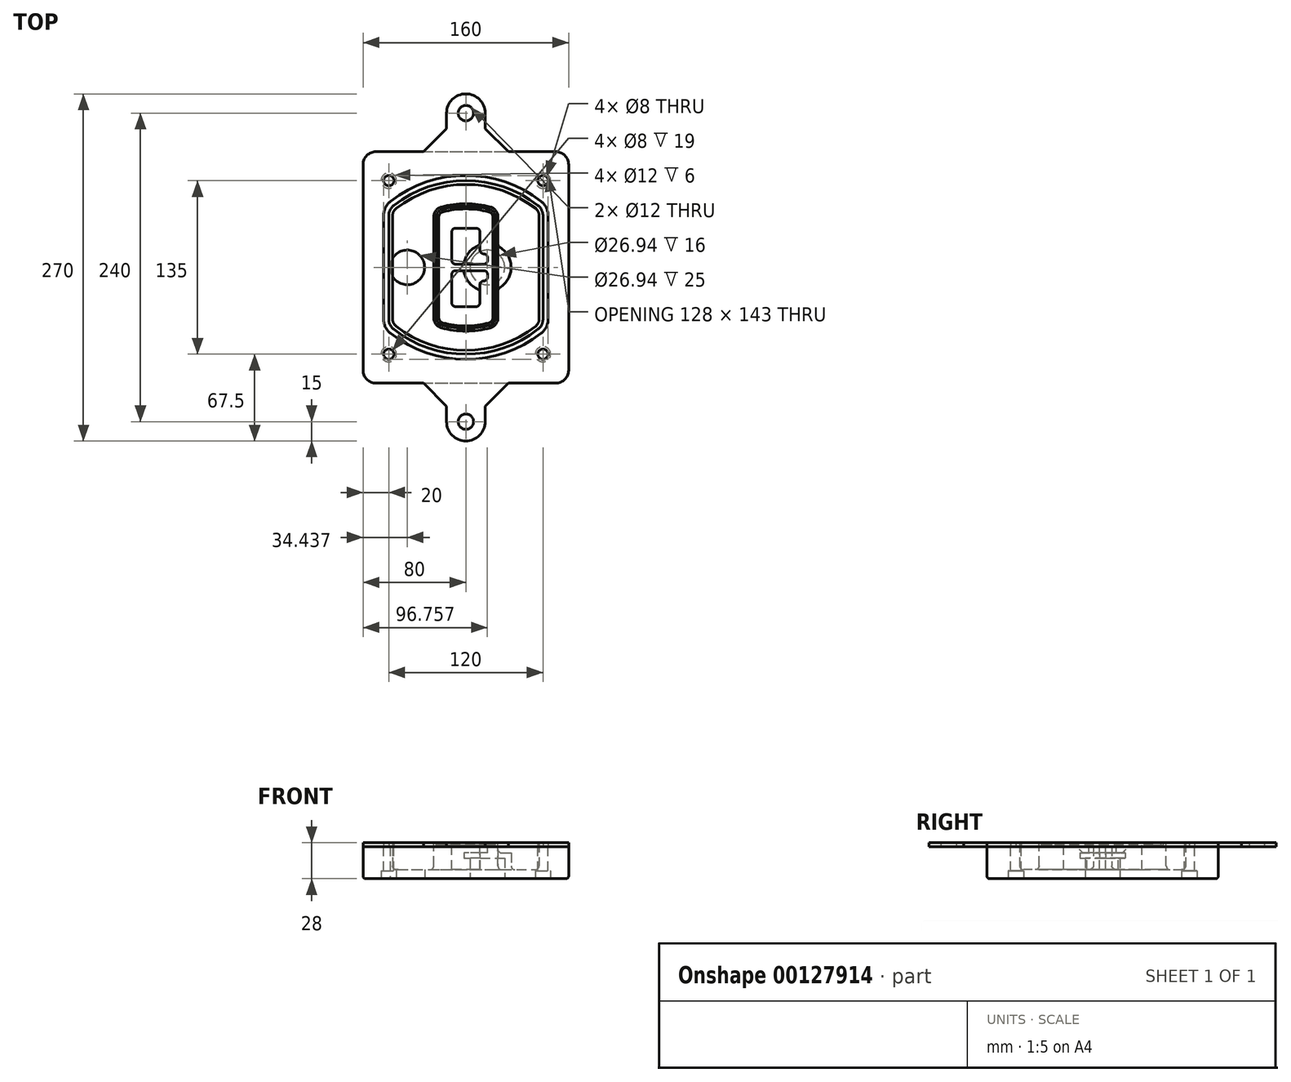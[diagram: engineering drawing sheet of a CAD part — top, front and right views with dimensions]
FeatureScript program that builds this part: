
annotation { "Feature Type Name" : "Feature", "Feature Type Description" : "" }
export const myFeature = defineFeature(function(context is Context, id is Id, definition is map)
    precondition{}
    {
        {
            var Q0;
            Q0=qCreatedBy(makeId("Top.planeOp"),FACE);
            var sketch = newSketch(context, id + "F0", { "sketchPlane" : qUnion([Q0])});
            skPoint(sketch, "E0.rect.middle", {"position": v(0, 0) * mm});
            skLineSegment(sketch, "E1.bottom", {"start": v(-70, -90) * mm, "end": v(70, -90) * mm});
            skLineSegment(sketch, "E1.top", {"start": v(-70, 90) * mm, "end": v(70, 90) * mm});
            skLineSegment(sketch, "E1.left", {"start": v(-80, -80) * mm, "end": v(-80, 80) * mm});
            skLineSegment(sketch, "E1.right", {"start": v(80, -80) * mm, "end": v(80, 80) * mm});
            skLineSegment(sketch, "E2", {"start": v(-80, 90) * mm, "end": v(80, -90) * mm, "construction": true});
            skLineSegment(sketch, "E3", {"start": v(80, 90) * mm, "end": v(-80, -90) * mm, "construction": true});
            skCircle(sketch, "E4", {"center": v(-60, 67.5) * mm, "radius": 4 * mm});
            skCircle(sketch, "E5", {"center": v(60, 67.5) * mm, "radius": 4 * mm});
            skCircle(sketch, "E6", {"center": v(60, -67.5) * mm, "radius": 4 * mm});
            skCircle(sketch, "E7", {"center": v(-60, -67.5) * mm, "radius": 4 * mm});
            skLineSegment(sketch, "E8", {"start": v(-60, 67.5) * mm, "end": v(60, 67.5) * mm, "construction": true});
            skLineSegment(sketch, "E9", {"start": v(60, 67.5) * mm, "end": v(60, -67.5) * mm, "construction": true});
            skLineSegment(sketch, "E10", {"start": v(60, -67.5) * mm, "end": v(-60, -67.5) * mm, "construction": true});
            skLineSegment(sketch, "E11", {"start": v(-60, -67.5) * mm, "end": v(-60, 67.5) * mm, "construction": true});
            skLineSegment(sketch, "E12", {"start": v(-60, 40.3) * mm, "end": v(-60, -40.3) * mm});
            skLineSegment(sketch, "E13", {"start": v(60, 40.3) * mm, "end": v(60, -40.3) * mm});
            skArc(sketch, "E14", {"start": v(56.15, 48.18) * mm, "mid": v(0, 67.5) * mm, "end": v(-56.15, 48.18) * mm});
            skArc(sketch, "E15", {"start": v(-56.15, -48.18) * mm, "mid": v(0, -67.5) * mm, "end": v(56.15, -48.18) * mm});
            skLineSegment(sketch, "E16", {"start": v(-60, 0) * mm, "end": v(60, 0) * mm, "construction": true});
            skPoint(sketch, "E17.visualSharp", {"position": v(-60, -45) * mm});
            skArc(sketch, "E17.filletArc", {"start": v(-60, -40.3) * mm, "mid": v(-58.99, -44.68) * mm, "end": v(-56.15, -48.18) * mm});
            skPoint(sketch, "E18.visualSharp", {"position": v(-60, 45) * mm});
            skArc(sketch, "E18.filletArc", {"start": v(-56.15, 48.18) * mm, "mid": v(-58.99, 44.68) * mm, "end": v(-60, 40.3) * mm});
            skPoint(sketch, "E19.visualSharp", {"position": v(60, 45) * mm});
            skArc(sketch, "E19.filletArc", {"start": v(60, 40.3) * mm, "mid": v(58.99, 44.68) * mm, "end": v(56.15, 48.18) * mm});
            skPoint(sketch, "E20.visualSharp", {"position": v(60, -45) * mm});
            skArc(sketch, "E20.filletArc", {"start": v(56.15, -48.18) * mm, "mid": v(58.99, -44.68) * mm, "end": v(60, -40.3) * mm});
            skPoint(sketch, "E21.visualSharp", {"position": v(-80, 90) * mm});
            skArc(sketch, "E21.filletArc", {"start": v(-70, 90) * mm, "mid": v(-77.07, 87.07) * mm, "end": v(-80, 80) * mm});
            skPoint(sketch, "E22.visualSharp", {"position": v(80, 90) * mm});
            skArc(sketch, "E22.filletArc", {"start": v(80, 80) * mm, "mid": v(77.07, 87.07) * mm, "end": v(70, 90) * mm});
            skPoint(sketch, "E23.visualSharp", {"position": v(80, -90) * mm});
            skArc(sketch, "E23.filletArc", {"start": v(70, -90) * mm, "mid": v(77.07, -87.07) * mm, "end": v(80, -80) * mm});
            skPoint(sketch, "E24.visualSharp", {"position": v(-80, -90) * mm});
            skArc(sketch, "E24.filletArc", {"start": v(-80, -80) * mm, "mid": v(-77.07, -87.07) * mm, "end": v(-70, -90) * mm});
            skArc(sketch, "E25.0", {"start": v(57, 40.3) * mm, "mid": v(56.3, 43.36) * mm, "end": v(54.3, 45.81) * mm});
            skLineSegment(sketch, "E25.1", {"start": v(57, 40.3) * mm, "end": v(57, -40.3) * mm});
            skArc(sketch, "E25.2", {"start": v(54.3, -45.81) * mm, "mid": v(56.3, -43.36) * mm, "end": v(57, -40.3) * mm});
            skArc(sketch, "E25.3", {"start": v(-54.3, -45.81) * mm, "mid": v(0, -64.5) * mm, "end": v(54.3, -45.81) * mm});
            skArc(sketch, "E25.4", {"start": v(-57, -40.3) * mm, "mid": v(-56.3, -43.36) * mm, "end": v(-54.3, -45.81) * mm});
            skArc(sketch, "E25.5", {"start": v(54.3, 45.81) * mm, "mid": v(0, 64.5) * mm, "end": v(-54.3, 45.81) * mm});
            skLineSegment(sketch, "E25.6", {"start": v(-57, 40.3) * mm, "end": v(-57, -40.3) * mm});
            skArc(sketch, "E25.7", {"start": v(-54.3, 45.81) * mm, "mid": v(-56.3, 43.36) * mm, "end": v(-57, 40.3) * mm});
            skArc(sketch, "E26.0", {"start": v(-58.62, 51.33) * mm, "mid": v(-62.58, 46.43) * mm, "end": v(-64, 40.3) * mm});
            skArc(sketch, "E26.1", {"start": v(58.62, 51.33) * mm, "mid": v(0, 71.5) * mm, "end": v(-58.62, 51.33) * mm});
            skArc(sketch, "E26.2", {"start": v(64, 40.3) * mm, "mid": v(62.58, 46.43) * mm, "end": v(58.62, 51.33) * mm});
            skLineSegment(sketch, "E26.3", {"start": v(64, 40.3) * mm, "end": v(64, -40.3) * mm});
            skArc(sketch, "E26.4", {"start": v(58.62, -51.33) * mm, "mid": v(62.58, -46.43) * mm, "end": v(64, -40.3) * mm});
            skLineSegment(sketch, "E26.5", {"start": v(-64, 40.3) * mm, "end": v(-64, -40.3) * mm});
            skArc(sketch, "E26.6", {"start": v(-58.62, -51.33) * mm, "mid": v(0, -71.5) * mm, "end": v(58.62, -51.33) * mm});
            skArc(sketch, "E26.7", {"start": v(-64, -40.3) * mm, "mid": v(-62.58, -46.43) * mm, "end": v(-58.62, -51.33) * mm});
            skSolve(sketch);
        }
        {
            var Q0;
            Q0=makeQuery(id+"F0.imprint","IMPRINT",FACE,{"disambiguationData":[TD([[makeQuery(id+"F0.imprint","IMPRINT",EDGE,{"derivedFrom":sQuery(id+"F0.wireOp",EDGE,"E1.bottom")}),1.0]])]});
            var Q1;
            Q1=makeQuery(id+"F0.imprint","IMPRINT",FACE,{"disambiguationData":[TD([[makeQuery(id+"F0.imprint","IMPRINT",EDGE,{"derivedFrom":sQuery(id+"F0.wireOp",EDGE,"E12")}),1.0]])]});
            var Q2;
            Q2=makeQuery(id+"F0.imprint","IMPRINT",FACE,{"disambiguationData":[TD([[makeQuery(id+"F0.imprint","IMPRINT",EDGE,{"derivedFrom":sQuery(id+"F0.wireOp",EDGE,"E25.0")}),1.0]])]});
            var Q3;
            Q3=makeQuery(id+"F0.imprint","IMPRINT",FACE,{"disambiguationData":[TD([[makeQuery(id+"F0.imprint","IMPRINT",EDGE,{"derivedFrom":sQuery(id+"F0.wireOp",EDGE,"E12")}),-1.0]])]});
            extrude(context, id + "F1", {"entities" : qUnion([Q0, Q1, Q2, Q3]), "oppositeDirection" : true, "depth" : 25 * mm});
        }
        {
            var Q0;
            Q0=makeQuery(id+"F0.imprint","IMPRINT",FACE,{"disambiguationData":[TD([[makeQuery(id+"F0.imprint","IMPRINT",EDGE,{"derivedFrom":sQuery(id+"F0.wireOp",EDGE,"E12")}),1.0]])]});
            extrude(context, id + "F2", {"entities" : qUnion([Q0]), "operationType" : NewBodyOperationType.ADD, "depth" : 3 * mm});
        }
        {
            var Q0;
            Q0=makeQuery(id+"F0.imprint","IMPRINT",FACE,{"disambiguationData":[TD([[makeQuery(id+"F0.imprint","IMPRINT",EDGE,{"derivedFrom":sQuery(id+"F0.wireOp",EDGE,"E25.0")}),1.0]])]});
            extrude(context, id + "F3", {"entities" : qUnion([Q0]), "operationType" : NewBodyOperationType.REMOVE, "oppositeDirection" : true, "depth" : 18 * mm});
        }
        {
            var Q0;
            Q0=makeQuery(id+"F2.opExtrude","CAP_FACE",FACE,{"disambiguationData":[OSD([sQuery(id+"F0.wireOp",EDGE,"E12"),sQuery(id+"F0.wireOp",EDGE,"E13"),sQuery(id+"F0.wireOp",EDGE,"E14"),sQuery(id+"F0.wireOp",EDGE,"E15"),sQuery(id+"F0.wireOp",EDGE,"E17.filletArc"),sQuery(id+"F0.wireOp",EDGE,"E18.filletArc"),sQuery(id+"F0.wireOp",EDGE,"E19.filletArc"),sQuery(id+"F0.wireOp",EDGE,"E20.filletArc"),sQuery(id+"F0.wireOp",EDGE,"E25.0"),sQuery(id+"F0.wireOp",EDGE,"E25.1"),sQuery(id+"F0.wireOp",EDGE,"E25.2"),sQuery(id+"F0.wireOp",EDGE,"E25.3"),sQuery(id+"F0.wireOp",EDGE,"E25.4"),sQuery(id+"F0.wireOp",EDGE,"E25.5"),sQuery(id+"F0.wireOp",EDGE,"E25.6"),sQuery(id+"F0.wireOp",EDGE,"E25.7")])],"isStart":false});
            var sketch = newSketch(context, id + "F4", { "sketchPlane" : qUnion([Q0])});
            skArc(sketch, "E27.0", {"start": v(-19.08, -46.97) * mm, "mid": v(0, -49.5) * mm, "end": v(19.08, -46.97) * mm});
            skArc(sketch, "E28.0", {"start": v(19.08, 46.97) * mm, "mid": v(0, 49.5) * mm, "end": v(-19.08, 46.97) * mm});
            skLineSegment(sketch, "E29", {"start": v(-25, 39.25) * mm, "end": v(-25, -39.25) * mm});
            skLineSegment(sketch, "E30", {"start": v(25, 39.25) * mm, "end": v(25, -39.25) * mm});
            skLineSegment(sketch, "E31", {"start": v(-25, 45.1) * mm, "end": v(25, 45.1) * mm, "construction": true});
            skLineSegment(sketch, "E32", {"start": v(-25, -45.1) * mm, "end": v(25, -45.1) * mm, "construction": true});
            skPoint(sketch, "E33.visualSharp", {"position": v(-25, 45.1) * mm});
            skArc(sketch, "E33.filletArc", {"start": v(-19.08, 46.97) * mm, "mid": v(-23.35, 44.11) * mm, "end": v(-25, 39.25) * mm});
            skPoint(sketch, "E34.visualSharp", {"position": v(25, 45.1) * mm});
            skArc(sketch, "E34.filletArc", {"start": v(25, 39.25) * mm, "mid": v(23.35, 44.11) * mm, "end": v(19.08, 46.97) * mm});
            skPoint(sketch, "E35.visualSharp", {"position": v(25, -45.1) * mm});
            skArc(sketch, "E35.filletArc", {"start": v(19.08, -46.97) * mm, "mid": v(23.35, -44.11) * mm, "end": v(25, -39.25) * mm});
            skPoint(sketch, "E36.visualSharp", {"position": v(-25, -45.1) * mm});
            skArc(sketch, "E36.filletArc", {"start": v(-25, -39.25) * mm, "mid": v(-23.35, -44.11) * mm, "end": v(-19.08, -46.97) * mm});
            skArc(sketch, "E37.0", {"start": v(54.3, 45.81) * mm, "mid": v(0, 64.5) * mm, "end": v(-54.3, 45.81) * mm});
            skArc(sketch, "E37.1", {"start": v(-54.3, 45.81) * mm, "mid": v(-56.3, 43.36) * mm, "end": v(-57, 40.3) * mm});
            skLineSegment(sketch, "E37.2", {"start": v(-57, 40.3) * mm, "end": v(-57, -40.3) * mm});
            skArc(sketch, "E37.3", {"start": v(-57, -40.3) * mm, "mid": v(-56.3, -43.36) * mm, "end": v(-54.3, -45.81) * mm});
            skArc(sketch, "E37.4", {"start": v(-54.3, -45.81) * mm, "mid": v(0, -64.5) * mm, "end": v(54.3, -45.81) * mm});
            skArc(sketch, "E37.5", {"start": v(54.3, -45.81) * mm, "mid": v(56.3, -43.36) * mm, "end": v(57, -40.3) * mm});
            skLineSegment(sketch, "E37.6", {"start": v(57, 40.3) * mm, "end": v(57, -40.3) * mm});
            skArc(sketch, "E37.7", {"start": v(57, 40.3) * mm, "mid": v(56.3, 43.36) * mm, "end": v(54.3, 45.81) * mm});
            skLineSegment(sketch, "E38.0", {"start": v(23, 39.25) * mm, "end": v(23, -39.25) * mm});
            skArc(sketch, "E38.1", {"start": v(18.56, -45.04) * mm, "mid": v(21.76, -42.9) * mm, "end": v(23, -39.25) * mm});
            skArc(sketch, "E38.2", {"start": v(-18.56, -45.04) * mm, "mid": v(0, -47.5) * mm, "end": v(18.56, -45.04) * mm});
            skArc(sketch, "E38.3", {"start": v(-23, -39.25) * mm, "mid": v(-21.76, -42.9) * mm, "end": v(-18.56, -45.04) * mm});
            skLineSegment(sketch, "E38.4", {"start": v(-23, 39.25) * mm, "end": v(-23, -39.25) * mm});
            skArc(sketch, "E38.5", {"start": v(23, 39.25) * mm, "mid": v(21.76, 42.9) * mm, "end": v(18.56, 45.04) * mm});
            skArc(sketch, "E38.6", {"start": v(-18.56, 45.04) * mm, "mid": v(-21.76, 42.9) * mm, "end": v(-23, 39.25) * mm});
            skArc(sketch, "E38.7", {"start": v(18.56, 45.04) * mm, "mid": v(0, 47.5) * mm, "end": v(-18.56, 45.04) * mm});
            skArc(sketch, "E39.0", {"start": v(21, 39.25) * mm, "mid": v(20.18, 41.68) * mm, "end": v(18.04, 43.1) * mm});
            skLineSegment(sketch, "E39.1", {"start": v(21, 39.25) * mm, "end": v(21, -39.25) * mm});
            skArc(sketch, "E39.2", {"start": v(18.04, -43.1) * mm, "mid": v(20.18, -41.68) * mm, "end": v(21, -39.25) * mm});
            skArc(sketch, "E39.3", {"start": v(-18.04, -43.1) * mm, "mid": v(0, -45.5) * mm, "end": v(18.04, -43.1) * mm});
            skArc(sketch, "E39.4", {"start": v(-21, -39.25) * mm, "mid": v(-20.18, -41.68) * mm, "end": v(-18.04, -43.1) * mm});
            skArc(sketch, "E39.5", {"start": v(18.04, 43.1) * mm, "mid": v(0, 45.5) * mm, "end": v(-18.04, 43.1) * mm});
            skLineSegment(sketch, "E39.6", {"start": v(-21, 39.25) * mm, "end": v(-21, -39.25) * mm});
            skArc(sketch, "E39.7", {"start": v(-18.04, 43.1) * mm, "mid": v(-20.18, 41.68) * mm, "end": v(-21, 39.25) * mm});
            skLineSegment(sketch, "E40", {"start": v(-25, 0) * mm, "end": v(25, 0) * mm, "construction": true});
            skLineSegment(sketch, "E41", {"start": v(-11, 5.5) * mm, "end": v(-11, 27.5) * mm});
            skLineSegment(sketch, "E42", {"start": v(-8, 30.5) * mm, "end": v(8, 30.5) * mm});
            skLineSegment(sketch, "E43", {"start": v(11, 27.5) * mm, "end": v(11, 13.5) * mm});
            skLineSegment(sketch, "E44", {"start": v(14, 10.5) * mm, "end": v(14, 10.5) * mm});
            skLineSegment(sketch, "E45", {"start": v(17, 7.5) * mm, "end": v(17, 5.5) * mm});
            skLineSegment(sketch, "E46", {"start": v(14, 2.5) * mm, "end": v(-8, 2.5) * mm});
            skPoint(sketch, "E47.visualSharp", {"position": v(-11, 30.5) * mm});
            skArc(sketch, "E47.filletArc", {"start": v(-8, 30.5) * mm, "mid": v(-10.12, 29.62) * mm, "end": v(-11, 27.5) * mm});
            skPoint(sketch, "E48.visualSharp", {"position": v(11, 30.5) * mm});
            skArc(sketch, "E48.filletArc", {"start": v(11, 27.5) * mm, "mid": v(10.12, 29.62) * mm, "end": v(8, 30.5) * mm});
            skPoint(sketch, "E49.visualSharp", {"position": v(11, 10.5) * mm});
            skArc(sketch, "E49.filletArc", {"start": v(11, 13.5) * mm, "mid": v(11.88, 11.38) * mm, "end": v(14, 10.5) * mm});
            skPoint(sketch, "E50.visualSharp", {"position": v(17, 10.5) * mm});
            skArc(sketch, "E50.filletArc", {"start": v(17, 7.5) * mm, "mid": v(16.12, 9.62) * mm, "end": v(14, 10.5) * mm});
            skPoint(sketch, "E51.visualSharp", {"position": v(17, 2.5) * mm});
            skArc(sketch, "E51.filletArc", {"start": v(14, 2.5) * mm, "mid": v(16.12, 3.38) * mm, "end": v(17, 5.5) * mm});
            skPoint(sketch, "E52.visualSharp", {"position": v(-11, 2.5) * mm});
            skArc(sketch, "E52.filletArc", {"start": v(-11, 5.5) * mm, "mid": v(-10.12, 3.38) * mm, "end": v(-8, 2.5) * mm});
            skLineSegment(sketch, "E53.0.MirrorCS", {"start": v(14, -2.5) * mm, "end": v(-8, -2.5) * mm});
            skArc(sketch, "E54.0.MirrorCS", {"start": v(-11, -5.5) * mm, "mid": v(-10.12, -3.38) * mm, "end": v(-8, -2.5) * mm});
            skLineSegment(sketch, "E55.0.MirrorCS", {"start": v(-11, -5.5) * mm, "end": v(-11, -27.5) * mm});
            skArc(sketch, "E56.0.MirrorCS", {"start": v(-8, -30.5) * mm, "mid": v(-10.12, -29.62) * mm, "end": v(-11, -27.5) * mm});
            skLineSegment(sketch, "E57.0.MirrorCS", {"start": v(-8, -30.5) * mm, "end": v(8, -30.5) * mm});
            skArc(sketch, "E58.0.MirrorCS", {"start": v(11, -27.5) * mm, "mid": v(10.12, -29.62) * mm, "end": v(8, -30.5) * mm});
            skLineSegment(sketch, "E59.0.MirrorCS", {"start": v(11, -27.5) * mm, "end": v(11, -13.5) * mm});
            skArc(sketch, "E60.0.MirrorCS", {"start": v(11, -13.5) * mm, "mid": v(11.88, -11.38) * mm, "end": v(14, -10.5) * mm});
            skArc(sketch, "E61.0.MirrorCS", {"start": v(17, -7.5) * mm, "mid": v(16.12, -9.62) * mm, "end": v(14, -10.5) * mm});
            skLineSegment(sketch, "E62.0.MirrorCS", {"start": v(17, -7.5) * mm, "end": v(17, -5.5) * mm});
            skArc(sketch, "E63.0.MirrorCS", {"start": v(14, -2.5) * mm, "mid": v(16.12, -3.38) * mm, "end": v(17, -5.5) * mm});
            skSolve(sketch);
        }
        {
            var Q0;
            Q0=makeQuery(id+"F4.imprint","IMPRINT",FACE,{"disambiguationData":[TD([[makeQuery(id+"F4.imprint","IMPRINT",EDGE,{"derivedFrom":sQuery(id+"F4.wireOp",EDGE,"E27.0")}),1.0]])]});
            var Q1;
            Q1=makeQuery(id+"F4.imprint","IMPRINT",FACE,{"disambiguationData":[TD([[makeQuery(id+"F4.imprint","IMPRINT",EDGE,{"derivedFrom":sQuery(id+"F4.wireOp",EDGE,"E38.0")}),-1.0]])]});
            var Q2;
            Q2=makeQuery(id+"F4.imprint","IMPRINT",FACE,{"disambiguationData":[TD([[makeQuery(id+"F4.imprint","IMPRINT",EDGE,{"derivedFrom":sQuery(id+"F4.wireOp",EDGE,"E39.0")}),1.0]])]});
            extrude(context, id + "F5", {"entities" : qUnion([Q0, Q1, Q2]), "operationType" : NewBodyOperationType.ADD, "endBound" : BoundingType.UP_TO_NEXT, "oppositeDirection" : true, "depth" : 25 * mm});
        }
        {
            var Q0;
            Q0=makeQuery(id+"F4.imprint","IMPRINT",FACE,{"disambiguationData":[TD([[makeQuery(id+"F4.imprint","IMPRINT",EDGE,{"derivedFrom":sQuery(id+"F4.wireOp",EDGE,"E38.0")}),-1.0]])]});
            extrude(context, id + "F6", {"entities" : qUnion([Q0]), "operationType" : NewBodyOperationType.REMOVE, "oppositeDirection" : true, "depth" : 2 * mm});
        }
        {
            var Q0;
            Q0=makeQuery(id+"F1.opExtrude","CAP_FACE",FACE,{"disambiguationData":[OSD([sQuery(id+"F0.wireOp",EDGE,"E1.bottom"),sQuery(id+"F0.wireOp",EDGE,"E1.top"),sQuery(id+"F0.wireOp",EDGE,"E1.left"),sQuery(id+"F0.wireOp",EDGE,"E1.right"),sQuery(id+"F0.wireOp",EDGE,"E4"),sQuery(id+"F0.wireOp",EDGE,"E5"),sQuery(id+"F0.wireOp",EDGE,"E6"),sQuery(id+"F0.wireOp",EDGE,"E7"),sQuery(id+"F0.wireOp",EDGE,"E21.filletArc"),sQuery(id+"F0.wireOp",EDGE,"E22.filletArc"),sQuery(id+"F0.wireOp",EDGE,"E23.filletArc"),sQuery(id+"F0.wireOp",EDGE,"E24.filletArc")])],"isStart":false});
            var sketch = newSketch(context, id + "F7", { "sketchPlane" : qUnion([Q0])});
            skCircle(sketch, "E64", {"center": v(16.76, 0) * mm, "radius": 13.47 * mm});
            skCircle(sketch, "E65", {"center": v(-45.56, 0) * mm, "radius": 13.47 * mm});
            skLineSegment(sketch, "E66", {"start": v(80, 0) * mm, "end": v(-80, 0) * mm});
            skCircle(sketch, "E67", {"center": v(16.76, 0) * mm, "radius": 18.47 * mm});
            skCircle(sketch, "E68", {"center": v(60, -67.5) * mm, "radius": 6 * mm});
            skCircle(sketch, "E69", {"center": v(-60, -67.5) * mm, "radius": 6 * mm});
            skCircle(sketch, "E70", {"center": v(-60, 67.5) * mm, "radius": 6 * mm});
            skCircle(sketch, "E71", {"center": v(60, 67.5) * mm, "radius": 6 * mm});
            skSolve(sketch);
        }
        {
            var Q0;
            {var subQ1=sQuery(id+"F7.wireOp",EDGE,"E66");var subQ4=sQuery(id+"F7.wireOp",EDGE,"E64");var subQ6=makeQuery(id+"F7.imprint","INTERSECT",VERTEX,{"disambiguationData":[OD(0.0)],"derivedFrom":[subQ4,subQ1]});Q0=makeQuery(id+"F7.imprint","IMPRINT",FACE,{"disambiguationData":[TD([[makeQuery(id+"F7.imprint","IMPRINT",EDGE,{"disambiguationData":[TD([[subQ6,-1.0]])],"derivedFrom":subQ4}),-1.0]])]});}
            var Q1;
            {var subQ0=sQuery(id+"F7.wireOp",EDGE,"E66");var subQ1=sQuery(id+"F7.wireOp",EDGE,"E64");var subQ3=makeQuery(id+"F7.imprint","INTERSECT",VERTEX,{"disambiguationData":[OD(0.0)],"derivedFrom":[subQ1,subQ0]});Q1=makeQuery(id+"F7.imprint","IMPRINT",FACE,{"disambiguationData":[TD([[makeQuery(id+"F7.imprint","IMPRINT",EDGE,{"disambiguationData":[TD([[subQ3,-1.0]])],"derivedFrom":subQ1}),1.0]])]});}
            var Q2;
            {var subQ0=sQuery(id+"F7.wireOp",EDGE,"E66");var subQ1=sQuery(id+"F7.wireOp",EDGE,"E64");var subQ3=makeQuery(id+"F7.imprint","INTERSECT",VERTEX,{"disambiguationData":[OD(0.0)],"derivedFrom":[subQ1,subQ0]});Q2=makeQuery(id+"F7.imprint","IMPRINT",FACE,{"disambiguationData":[TD([[makeQuery(id+"F7.imprint","IMPRINT",EDGE,{"disambiguationData":[TD([[subQ3,1.0]])],"derivedFrom":subQ1}),1.0]])]});}
            var Q3;
            {var subQ1=sQuery(id+"F7.wireOp",EDGE,"E66");var subQ4=sQuery(id+"F7.wireOp",EDGE,"E64");var subQ6=makeQuery(id+"F7.imprint","INTERSECT",VERTEX,{"disambiguationData":[OD(0.0)],"derivedFrom":[subQ4,subQ1]});Q3=makeQuery(id+"F7.imprint","IMPRINT",FACE,{"disambiguationData":[TD([[makeQuery(id+"F7.imprint","IMPRINT",EDGE,{"disambiguationData":[TD([[subQ6,1.0]])],"derivedFrom":subQ4}),-1.0]])]});}
            extrude(context, id + "F8", {"entities" : qUnion([Q0, Q1, Q2, Q3]), "operationType" : NewBodyOperationType.ADD, "oppositeDirection" : true, "depth" : 20 * mm});
        }
        {
            var Q0;
            {var subQ0=sQuery(id+"F7.wireOp",EDGE,"E66");var subQ1=sQuery(id+"F7.wireOp",EDGE,"E64");var subQ3=makeQuery(id+"F7.imprint","INTERSECT",VERTEX,{"disambiguationData":[OD(0.0)],"derivedFrom":[subQ1,subQ0]});Q0=makeQuery(id+"F7.imprint","IMPRINT",FACE,{"disambiguationData":[TD([[makeQuery(id+"F7.imprint","IMPRINT",EDGE,{"disambiguationData":[TD([[subQ3,-1.0]])],"derivedFrom":subQ1}),1.0]])]});}
            var Q1;
            {var subQ0=sQuery(id+"F7.wireOp",EDGE,"E66");var subQ1=sQuery(id+"F7.wireOp",EDGE,"E64");var subQ3=makeQuery(id+"F7.imprint","INTERSECT",VERTEX,{"disambiguationData":[OD(0.0)],"derivedFrom":[subQ1,subQ0]});Q1=makeQuery(id+"F7.imprint","IMPRINT",FACE,{"disambiguationData":[TD([[makeQuery(id+"F7.imprint","IMPRINT",EDGE,{"disambiguationData":[TD([[subQ3,1.0]])],"derivedFrom":subQ1}),1.0]])]});}
            extrude(context, id + "F9", {"entities" : qUnion([Q0, Q1]), "operationType" : NewBodyOperationType.REMOVE, "oppositeDirection" : true, "depth" : 16 * mm});
        }
        {
            var Q0;
            {var subQ0=sQuery(id+"F7.wireOp",EDGE,"E66");var subQ1=sQuery(id+"F7.wireOp",EDGE,"E65");var subQ3=makeQuery(id+"F7.imprint","INTERSECT",VERTEX,{"disambiguationData":[OD(0.0)],"derivedFrom":[subQ1,subQ0]});Q0=makeQuery(id+"F7.imprint","IMPRINT",FACE,{"disambiguationData":[TD([[makeQuery(id+"F7.imprint","IMPRINT",EDGE,{"disambiguationData":[TD([[subQ3,-1.0]])],"derivedFrom":subQ1}),1.0]])]});}
            var Q1;
            {var subQ0=sQuery(id+"F7.wireOp",EDGE,"E66");var subQ1=sQuery(id+"F7.wireOp",EDGE,"E65");var subQ3=makeQuery(id+"F7.imprint","INTERSECT",VERTEX,{"disambiguationData":[OD(0.0)],"derivedFrom":[subQ1,subQ0]});Q1=makeQuery(id+"F7.imprint","IMPRINT",FACE,{"disambiguationData":[TD([[makeQuery(id+"F7.imprint","IMPRINT",EDGE,{"disambiguationData":[TD([[subQ3,1.0]])],"derivedFrom":subQ1}),1.0]])]});}
            extrude(context, id + "F10", {"entities" : qUnion([Q0, Q1]), "operationType" : NewBodyOperationType.REMOVE, "oppositeDirection" : true, "depth" : 25 * mm});
        }
        {
            var Q0;
            Q0=makeQuery(id+"F7.imprint","IMPRINT",FACE,{"disambiguationData":[TD([[makeQuery(id+"F7.imprint","IMPRINT",EDGE,{"derivedFrom":sQuery(id+"F7.wireOp",EDGE,"E68")}),1.0]])]});
            var Q1;
            Q1=makeQuery(id+"F7.imprint","IMPRINT",FACE,{"disambiguationData":[TD([[makeQuery(id+"F7.imprint","IMPRINT",EDGE,{"derivedFrom":makeQuery(id+"F1.opExtrude","CAP_EDGE",EDGE,{"disambiguationData":[OSD([sQuery(id+"F0.wireOp",EDGE,"E5")])],"isStart":false})}),-1.0]])]});
            var Q2;
            Q2=makeQuery(id+"F7.imprint","IMPRINT",FACE,{"disambiguationData":[TD([[makeQuery(id+"F7.imprint","IMPRINT",EDGE,{"derivedFrom":sQuery(id+"F7.wireOp",EDGE,"E69")}),1.0]])]});
            var Q3;
            Q3=makeQuery(id+"F7.imprint","IMPRINT",FACE,{"disambiguationData":[TD([[makeQuery(id+"F7.imprint","IMPRINT",EDGE,{"derivedFrom":makeQuery(id+"F1.opExtrude","CAP_EDGE",EDGE,{"disambiguationData":[OSD([sQuery(id+"F0.wireOp",EDGE,"E4")])],"isStart":false})}),-1.0]])]});
            var Q4;
            Q4=makeQuery(id+"F7.imprint","IMPRINT",FACE,{"disambiguationData":[TD([[makeQuery(id+"F7.imprint","IMPRINT",EDGE,{"derivedFrom":sQuery(id+"F7.wireOp",EDGE,"E70")}),1.0]])]});
            var Q5;
            Q5=makeQuery(id+"F7.imprint","IMPRINT",FACE,{"disambiguationData":[TD([[makeQuery(id+"F7.imprint","IMPRINT",EDGE,{"derivedFrom":makeQuery(id+"F1.opExtrude","CAP_EDGE",EDGE,{"disambiguationData":[OSD([sQuery(id+"F0.wireOp",EDGE,"E7")])],"isStart":false})}),-1.0]])]});
            var Q6;
            Q6=makeQuery(id+"F7.imprint","IMPRINT",FACE,{"disambiguationData":[TD([[makeQuery(id+"F7.imprint","IMPRINT",EDGE,{"derivedFrom":sQuery(id+"F7.wireOp",EDGE,"E71")}),1.0]])]});
            var Q7;
            Q7=makeQuery(id+"F7.imprint","IMPRINT",FACE,{"disambiguationData":[TD([[makeQuery(id+"F7.imprint","IMPRINT",EDGE,{"derivedFrom":makeQuery(id+"F1.opExtrude","CAP_EDGE",EDGE,{"disambiguationData":[OSD([sQuery(id+"F0.wireOp",EDGE,"E6")])],"isStart":false})}),-1.0]])]});
            extrude(context, id + "F11", {"entities" : qUnion([Q0, Q1, Q2, Q3, Q4, Q5, Q6, Q7]), "operationType" : NewBodyOperationType.REMOVE, "oppositeDirection" : true, "depth" : 6 * mm});
        }
        {
            var Q0;
            Q0=makeQuery(id+"F9.boolean.opBoolean","COPY",FACE,{"derivedFrom":makeQuery(id+"F9.opExtrude","CAP_FACE",FACE,{"disambiguationData":[OSD([sQuery(id+"F7.wireOp",EDGE,"E64")])],"isStart":false})});
            var sketch = newSketch(context, id + "F12", { "sketchPlane" : qUnion([Q0])});
            skArc(sketch, "E72.0", {"start": v(11, 17.55) * mm, "mid": v(2.57, 11.82) * mm, "end": v(-1.54, 2.5) * mm});
            skArc(sketch, "E72.1", {"start": v(-1.54, -2.5) * mm, "mid": v(2.57, -11.82) * mm, "end": v(11, -17.55) * mm});
            skLineSegment(sketch, "E73", {"start": v(-1.54, -2.5) * mm, "end": v(14, -2.5) * mm});
            skLineSegment(sketch, "E74.0", {"start": v(14, 2.5) * mm, "end": v(-1.54, 2.5) * mm});
            skArc(sketch, "E74.1", {"start": v(14, 2.5) * mm, "mid": v(16.12, 3.38) * mm, "end": v(17, 5.5) * mm});
            skLineSegment(sketch, "E74.2", {"start": v(17, 7.5) * mm, "end": v(17, 5.5) * mm});
            skArc(sketch, "E74.3", {"start": v(17, 7.5) * mm, "mid": v(16.12, 9.62) * mm, "end": v(14, 10.5) * mm});
            skArc(sketch, "E74.4", {"start": v(11, 13.5) * mm, "mid": v(11.88, 11.38) * mm, "end": v(14, 10.5) * mm});
            skLineSegment(sketch, "E74.5", {"start": v(11, 17.55) * mm, "end": v(11, 13.5) * mm});
            skLineSegment(sketch, "E74.7", {"start": v(14, -2.5) * mm, "end": v(-1.54, -2.5) * mm});
            skArc(sketch, "E74.8", {"start": v(14, -2.5) * mm, "mid": v(16.12, -3.38) * mm, "end": v(17, -5.5) * mm});
            skLineSegment(sketch, "E74.9", {"start": v(17, -7.5) * mm, "end": v(17, -5.5) * mm});
            skArc(sketch, "E74.10", {"start": v(17, -7.5) * mm, "mid": v(16.12, -9.62) * mm, "end": v(14, -10.5) * mm});
            skArc(sketch, "E74.11", {"start": v(11, -13.5) * mm, "mid": v(11.88, -11.38) * mm, "end": v(14, -10.5) * mm});
            skLineSegment(sketch, "E74.12", {"start": v(11, -17.55) * mm, "end": v(11, -13.5) * mm});
            skPoint(sketch, "E75.orphan", {"position": v(11, -27.5) * mm});
            skPoint(sketch, "E76.orphan", {"position": v(-8, -2.5) * mm});
            skPoint(sketch, "E77.orphan", {"position": v(-8, 2.5) * mm});
            skPoint(sketch, "E78.orphan", {"position": v(11, 27.5) * mm});
            skSolve(sketch);
        }
        {
            var Q0;
            {var subQ7=sQuery(id+"F12.wireOp",EDGE,"E72.0");var subQ14=sQuery(id+"F12.wireOp",EDGE,"E72.1");var subQ16=sQuery(id+"F12.wireOp",EDGE,"E74.1");var subQ18=sQuery(id+"F12.wireOp",EDGE,"E74.8");Q0=qUnion([makeQuery(id+"F12.imprint","IMPRINT",FACE,{"disambiguationData":[TD([[makeQuery(id+"F12.imprint","IMPRINT",EDGE,{"derivedFrom":subQ7}),1.0]])]}),makeQuery(id+"F12.imprint","IMPRINT",FACE,{"disambiguationData":[TD([[makeQuery(id+"F12.imprint","IMPRINT",EDGE,{"derivedFrom":subQ14}),1.0]])]}),makeQuery(id+"F12.imprint","IMPRINT",FACE,{"disambiguationData":[TD([[makeQuery(id+"F12.imprint","IMPRINT",EDGE,{"derivedFrom":subQ16}),1.0]])]}),makeQuery(id+"F12.imprint","IMPRINT",FACE,{"disambiguationData":[TD([[makeQuery(id+"F12.imprint","IMPRINT",EDGE,{"derivedFrom":subQ18}),-1.0]])]})]);}
            var Q1;
            Q1=makeQuery(id+"F5.boolean.opBoolean","SPLIT",FACE,{"disambiguationData":[TD([makeQuery(id+"F5.opExtrude","SWEPT_FACE",FACE,{"disambiguationData":[OSD([sQuery(id+"F4.wireOp",EDGE,"E41")])]})])],"derivedFrom":makeQuery(id+"F3.boolean.opBoolean","COPY",FACE,{"derivedFrom":makeQuery(id+"F3.opExtrude","CAP_FACE",FACE,{"disambiguationData":[OSD([sQuery(id+"F0.wireOp",EDGE,"E25.0"),sQuery(id+"F0.wireOp",EDGE,"E25.1"),sQuery(id+"F0.wireOp",EDGE,"E25.2"),sQuery(id+"F0.wireOp",EDGE,"E25.3"),sQuery(id+"F0.wireOp",EDGE,"E25.4"),sQuery(id+"F0.wireOp",EDGE,"E25.5"),sQuery(id+"F0.wireOp",EDGE,"E25.6"),sQuery(id+"F0.wireOp",EDGE,"E25.7")])],"isStart":false})})});
            extrude(context, id + "F13", {"entities" : qUnion([Q0]), "operationType" : NewBodyOperationType.REMOVE, "endBound" : BoundingType.UP_TO_SURFACE, "endBoundEntityFace" : qUnion([Q1]), "depth" : 25 * mm});
        }
        {
            var Q0;
            Q0=makeQuery(id+"F3.boolean.opBoolean","COPY",EDGE,{"derivedFrom":makeQuery(id+"F3.opExtrude","CAP_EDGE",EDGE,{"disambiguationData":[OSD([sQuery(id+"F0.wireOp",EDGE,"E25.6")])],"isStart":false})});
            var Q1;
            Q1=makeQuery(id+"F8.boolean.opBoolean","INTERSECT",EDGE,{"derivedFrom":[makeQuery(id+"F5.opExtrude","SWEPT_FACE",FACE,{"disambiguationData":[OSD([sQuery(id+"F4.wireOp",EDGE,"E30")])]}),makeQuery(id+"F8.opExtrude","CAP_FACE",FACE,{"disambiguationData":[OSD([sQuery(id+"F7.wireOp",EDGE,"E67")])],"isStart":false})]});
            var Q2;
            Q2=makeQuery(id+"F8.boolean.opBoolean","INTERSECT",EDGE,{"disambiguationData":[OD(1.0)],"derivedFrom":[makeQuery(id+"F5.opExtrude","SWEPT_FACE",FACE,{"disambiguationData":[OSD([sQuery(id+"F4.wireOp",EDGE,"E30")])]}),makeQuery(id+"F8.opExtrude","SWEPT_FACE",FACE,{"disambiguationData":[OSD([sQuery(id+"F7.wireOp",EDGE,"E67")])]})]});
            var Q3;
            {var subQ0=sQuery(id+"F4.wireOp",EDGE,"E30");Q3=makeQuery(id+"F8.boolean.opBoolean","SPLIT",EDGE,{"disambiguationData":[TD([makeQuery(id+"F5.opExtrude","SWEPT_FACE",FACE,{"disambiguationData":[OSD([sQuery(id+"F4.wireOp",EDGE,"E35.filletArc")])]})])],"derivedFrom":makeQuery(id+"F5.opExtrude","CAP_EDGE",EDGE,{"disambiguationData":[OSD([subQ0])],"isStart":false})});}
            var Q4;
            {var subQ0=sQuery(id+"F0.wireOp",EDGE,"E25.7");var subQ1=sQuery(id+"F0.wireOp",EDGE,"E25.1");var subQ2=sQuery(id+"F0.wireOp",EDGE,"E25.6");var subQ3=sQuery(id+"F0.wireOp",EDGE,"E25.5");var subQ4=sQuery(id+"F0.wireOp",EDGE,"E25.4");var subQ5=sQuery(id+"F0.wireOp",EDGE,"E25.0");var subQ6=sQuery(id+"F0.wireOp",EDGE,"E25.2");var subQ7=sQuery(id+"F0.wireOp",EDGE,"E25.3");Q4=makeQuery(id+"F8.boolean.opBoolean","INTERSECT",EDGE,{"derivedFrom":[makeQuery(id+"F5.boolean.opBoolean","SPLIT",FACE,{"disambiguationData":[TD([makeQuery(id+"F2.opExtrude","SWEPT_FACE",FACE,{"disambiguationData":[OSD([subQ5])]})])],"derivedFrom":makeQuery(id+"F3.boolean.opBoolean","COPY",FACE,{"derivedFrom":makeQuery(id+"F3.opExtrude","CAP_FACE",FACE,{"disambiguationData":[OSD([subQ5,subQ1,subQ6,subQ7,subQ4,subQ3,subQ2,subQ0])],"isStart":false})})}),makeQuery(id+"F8.opExtrude","SWEPT_FACE",FACE,{"disambiguationData":[OSD([sQuery(id+"F7.wireOp",EDGE,"E67")])]})]});}
            var Q5;
            Q5=makeQuery(id+"F8.boolean.opBoolean","INTERSECT",EDGE,{"disambiguationData":[OD(0.0)],"derivedFrom":[makeQuery(id+"F5.opExtrude","SWEPT_FACE",FACE,{"disambiguationData":[OSD([sQuery(id+"F4.wireOp",EDGE,"E30")])]}),makeQuery(id+"F8.opExtrude","SWEPT_FACE",FACE,{"disambiguationData":[OSD([sQuery(id+"F7.wireOp",EDGE,"E67")])]})]});
            fillet(context, id + "F14", {"entities" : qUnion([Q0, Q1, Q2, Q3, Q4, Q5]), "radius" : 3 * mm, "tangentPropagation" : true, "allowEdgeOverflow" : false});
        }
        {
            var Q0;
            Q0=makeQuery(id+"F1.opExtrude","CAP_EDGE",EDGE,{"disambiguationData":[OSD([sQuery(id+"F0.wireOp",EDGE,"E1.bottom")])],"isStart":false});
            fillet(context, id + "F15", {"entities" : qUnion([Q0]), "radius" : 2 * mm, "tangentPropagation" : true, "allowEdgeOverflow" : false});
        }
        {
            var Q0;
            Q0=makeQuery(id+"F0.imprint","IMPRINT",FACE,{"disambiguationData":[TD([[makeQuery(id+"F0.imprint","IMPRINT",EDGE,{"derivedFrom":sQuery(id+"F0.wireOp",EDGE,"E1.bottom")}),1.0]])]});
            var sketch = newSketch(context, id + "F16", { "sketchPlane" : qUnion([Q0])});
            skLineSegment(sketch, "E79", {"start": v(0, 90) * mm, "end": v(0, 120) * mm, "construction": true});
            skCircle(sketch, "E80", {"center": v(0, 120) * mm, "radius": 6 * mm});
            skLineSegment(sketch, "E81", {"start": v(-15, 120) * mm, "end": v(-15, 108) * mm});
            skLineSegment(sketch, "E82", {"start": v(-15, 108) * mm, "end": v(-33, 90) * mm});
            skLineSegment(sketch, "E83.MirrorCS", {"start": v(15, 120) * mm, "end": v(15, 108) * mm});
            skLineSegment(sketch, "E84.MirrorCS", {"start": v(15, 108) * mm, "end": v(33, 90) * mm});
            skArc(sketch, "E85", {"start": v(15, 120) * mm, "mid": v(0, 135) * mm, "end": v(-15, 120) * mm});
            skArc(sketch, "E86.0", {"start": v(59.97, 40.3) * mm, "mid": v(58.96, 44.67) * mm, "end": v(56.14, 48.15) * mm});
            skLineSegment(sketch, "E86.1", {"start": v(59.97, 40.3) * mm, "end": v(59.97, -40.3) * mm});
            skArc(sketch, "E86.2", {"start": v(56.14, 48.15) * mm, "mid": v(0, 67.47) * mm, "end": v(-56.14, 48.15) * mm});
            skArc(sketch, "E86.3", {"start": v(56.14, -48.15) * mm, "mid": v(58.96, -44.67) * mm, "end": v(59.97, -40.3) * mm});
            skArc(sketch, "E86.4", {"start": v(-56.14, 48.15) * mm, "mid": v(-58.96, 44.67) * mm, "end": v(-59.97, 40.3) * mm});
            skLineSegment(sketch, "E86.5", {"start": v(-59.97, 40.3) * mm, "end": v(-59.97, -40.3) * mm});
            skArc(sketch, "E86.6", {"start": v(-59.97, -40.3) * mm, "mid": v(-58.96, -44.67) * mm, "end": v(-56.14, -48.15) * mm});
            skArc(sketch, "E86.7", {"start": v(-56.14, -48.15) * mm, "mid": v(0, -67.47) * mm, "end": v(56.14, -48.15) * mm});
            skLineSegment(sketch, "E87", {"start": v(90.23, 0) * mm, "end": v(-112.11, 0) * mm, "construction": true});
            skLineSegment(sketch, "E88.MirrorCS", {"start": v(-15, -108) * mm, "end": v(-33, -90) * mm});
            skLineSegment(sketch, "E89.MirrorCS", {"start": v(15, -108) * mm, "end": v(33, -90) * mm});
            skLineSegment(sketch, "E90.MirrorCS", {"start": v(15, -120) * mm, "end": v(15, -108) * mm});
            skLineSegment(sketch, "E91.MirrorCS", {"start": v(-15, -120) * mm, "end": v(-15, -108) * mm});
            skArc(sketch, "E92.MirrorCS", {"start": v(15, -120) * mm, "mid": v(0, -135) * mm, "end": v(-15, -120) * mm});
            skCircle(sketch, "E93.MirrorC", {"center": v(0, -120) * mm, "radius": 6 * mm});
            skSolve(sketch);
        }
        {
            var Q0;
            {var subQ0=sQuery(id+"F16.wireOp",EDGE,"E88.MirrorCS");Q0=makeQuery(id+"F16.imprint","IMPRINT",FACE,{"disambiguationData":[TD([[makeQuery(id+"F16.imprint","IMPRINT",EDGE,{"derivedFrom":subQ0}),-1.0]])]});}
            var Q1;
            Q1=makeQuery(id+"F16.imprint","IMPRINT",FACE,{"disambiguationData":[TD([[makeQuery(id+"F16.imprint","IMPRINT",EDGE,{"derivedFrom":makeQuery(id+"F0.imprint","IMPRINT",EDGE,{"derivedFrom":sQuery(id+"F0.wireOp",EDGE,"E1.left")})}),-1.0]])]});
            var Q2;
            Q2=makeQuery(id+"F16.imprint","IMPRINT",FACE,{"disambiguationData":[TD([[makeQuery(id+"F16.imprint","IMPRINT",EDGE,{"derivedFrom":sQuery(id+"F16.wireOp",EDGE,"E80")}),-1.0]])]});
            var Q3;
            {var subQ0=sQuery(id+"F4.wireOp",EDGE,"E63.0.MirrorCS");var subQ1=sQuery(id+"F4.wireOp",EDGE,"E62.0.MirrorCS");var subQ2=sQuery(id+"F4.wireOp",EDGE,"E61.0.MirrorCS");var subQ3=sQuery(id+"F4.wireOp",EDGE,"E60.0.MirrorCS");var subQ4=sQuery(id+"F4.wireOp",EDGE,"E59.0.MirrorCS");var subQ5=sQuery(id+"F4.wireOp",EDGE,"E58.0.MirrorCS");var subQ6=sQuery(id+"F4.wireOp",EDGE,"E57.0.MirrorCS");var subQ7=sQuery(id+"F4.wireOp",EDGE,"E56.0.MirrorCS");var subQ8=sQuery(id+"F4.wireOp",EDGE,"E55.0.MirrorCS");var subQ9=sQuery(id+"F4.wireOp",EDGE,"E54.0.MirrorCS");var subQ10=sQuery(id+"F4.wireOp",EDGE,"E53.0.MirrorCS");var subQ11=sQuery(id+"F4.wireOp",EDGE,"E52.filletArc");var subQ12=sQuery(id+"F4.wireOp",EDGE,"E45");var subQ13=sQuery(id+"F4.wireOp",EDGE,"E43");var subQ14=sQuery(id+"F4.wireOp",EDGE,"E42");var subQ15=sQuery(id+"F4.wireOp",EDGE,"E41");var subQ16=sQuery(id+"F4.wireOp",EDGE,"E46");var subQ17=sQuery(id+"F4.wireOp",EDGE,"E47.filletArc");var subQ18=sQuery(id+"F4.wireOp",EDGE,"E48.filletArc");var subQ19=sQuery(id+"F4.wireOp",EDGE,"E49.filletArc");var subQ20=sQuery(id+"F4.wireOp",EDGE,"E50.filletArc");var subQ21=sQuery(id+"F4.wireOp",EDGE,"E51.filletArc");Q3=makeQuery(id+"F6.boolean.opBoolean","SPLIT",FACE,{"disambiguationData":[TD([makeQuery(id+"F5.opExtrude","SWEPT_FACE",FACE,{"disambiguationData":[OSD([subQ15])]})])],"derivedFrom":makeQuery(id+"F5.opExtrude","CAP_FACE",FACE,{"disambiguationData":[OSD([sQuery(id+"F4.wireOp",EDGE,"E27.0"),sQuery(id+"F4.wireOp",EDGE,"E28.0"),sQuery(id+"F4.wireOp",EDGE,"E29"),sQuery(id+"F4.wireOp",EDGE,"E30"),sQuery(id+"F4.wireOp",EDGE,"E33.filletArc"),sQuery(id+"F4.wireOp",EDGE,"E34.filletArc"),sQuery(id+"F4.wireOp",EDGE,"E35.filletArc"),sQuery(id+"F4.wireOp",EDGE,"E36.filletArc"),subQ15,subQ14,subQ13,subQ12,subQ16,subQ17,subQ18,subQ19,subQ20,subQ21,subQ11,subQ10,subQ9,subQ8,subQ7,subQ6,subQ5,subQ4,subQ3,subQ2,subQ1,subQ0])],"isStart":true})});}
            extrude(context, id + "F17", {"entities" : qUnion([Q0, Q1, Q2]), "endBound" : BoundingType.UP_TO_SURFACE, "endBoundEntityFace" : qUnion([Q3]), "depth" : 25 * mm});
        }
    });
